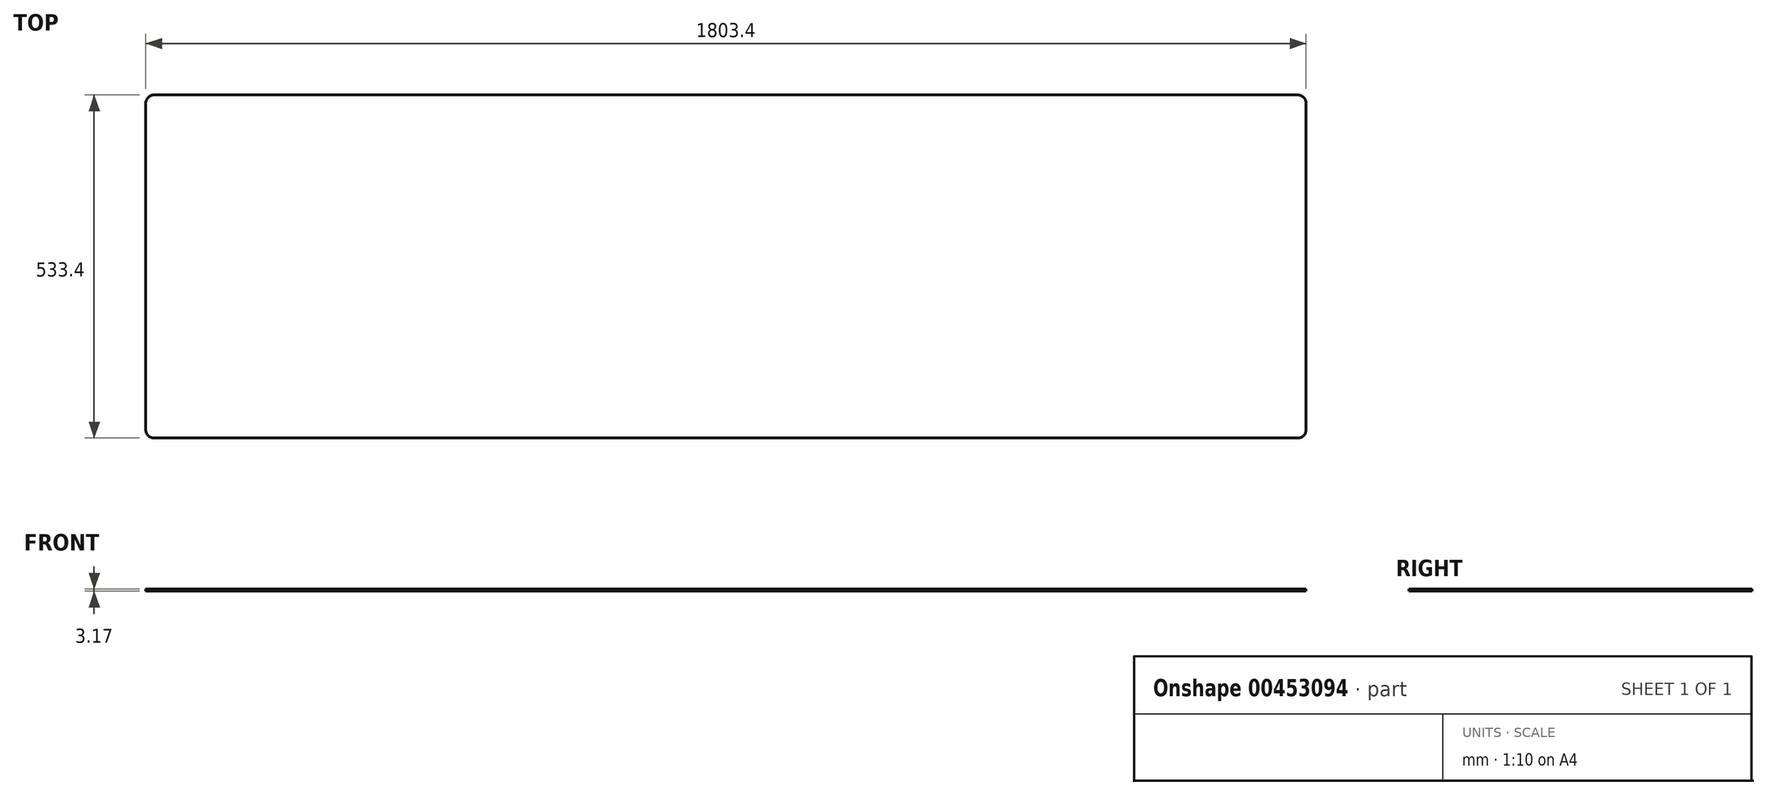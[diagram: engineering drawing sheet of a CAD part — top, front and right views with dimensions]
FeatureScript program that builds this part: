
annotation { "Feature Type Name" : "Feature", "Feature Type Description" : "" }
export const myFeature = defineFeature(function(context is Context, id is Id, definition is map)
    precondition{}
    {
        {
            var Q0;
            Q0=qCreatedBy(makeId("Top.planeOp"),FACE);
            var sketch = newSketch(context, id + "F0", { "sketchPlane" : qUnion([Q0])});
            skLineSegment(sketch, "E0.bottom", {"start": v(901.7, 266.7) * mm, "end": v(-901.7, 266.7) * mm});
            skLineSegment(sketch, "E0.top", {"start": v(901.7, -266.7) * mm, "end": v(-901.7, -266.7) * mm});
            skLineSegment(sketch, "E0.left", {"start": v(901.7, 266.7) * mm, "end": v(901.7, -266.7) * mm});
            skLineSegment(sketch, "E0.right", {"start": v(-901.7, 266.7) * mm, "end": v(-901.7, -266.7) * mm});
            skPoint(sketch, "E0.middle", {"position": v(0, 0) * mm});
            skSolve(sketch);
        }
        {
            var Q0;
            Q0 = qSketchRegion(id + "F0", true);
            extrude(context, id + "F1", {"entities" : qUnion([Q0]), "depth" : 3.17 * mm});
        }
        {
            var Q0;
            Q0=makeQuery(id+"F1.opExtrude","SWEPT_EDGE",EDGE,{"disambiguationData":[OSD([sQuery(id+"F0.wireOp",EDGE,"E0.top"),sQuery(id+"F0.wireOp",EDGE,"E0.right")])]});
            var Q1;
            Q1=makeQuery(id+"F1.opExtrude","SWEPT_EDGE",EDGE,{"disambiguationData":[OSD([sQuery(id+"F0.wireOp",EDGE,"E0.bottom"),sQuery(id+"F0.wireOp",EDGE,"E0.right")])]});
            var Q2;
            Q2=makeQuery(id+"F1.opExtrude","SWEPT_EDGE",EDGE,{"disambiguationData":[OSD([sQuery(id+"F0.wireOp",EDGE,"E0.bottom"),sQuery(id+"F0.wireOp",EDGE,"E0.left")])]});
            var Q3;
            Q3=makeQuery(id+"F1.opExtrude","SWEPT_EDGE",EDGE,{"disambiguationData":[OSD([sQuery(id+"F0.wireOp",EDGE,"E0.top"),sQuery(id+"F0.wireOp",EDGE,"E0.left")])]});
            fillet(context, id + "F2", {"entities" : qUnion([Q0, Q1, Q2, Q3]), "radius" : 12.7 * mm, "allowEdgeOverflow" : false});
        }
    });
